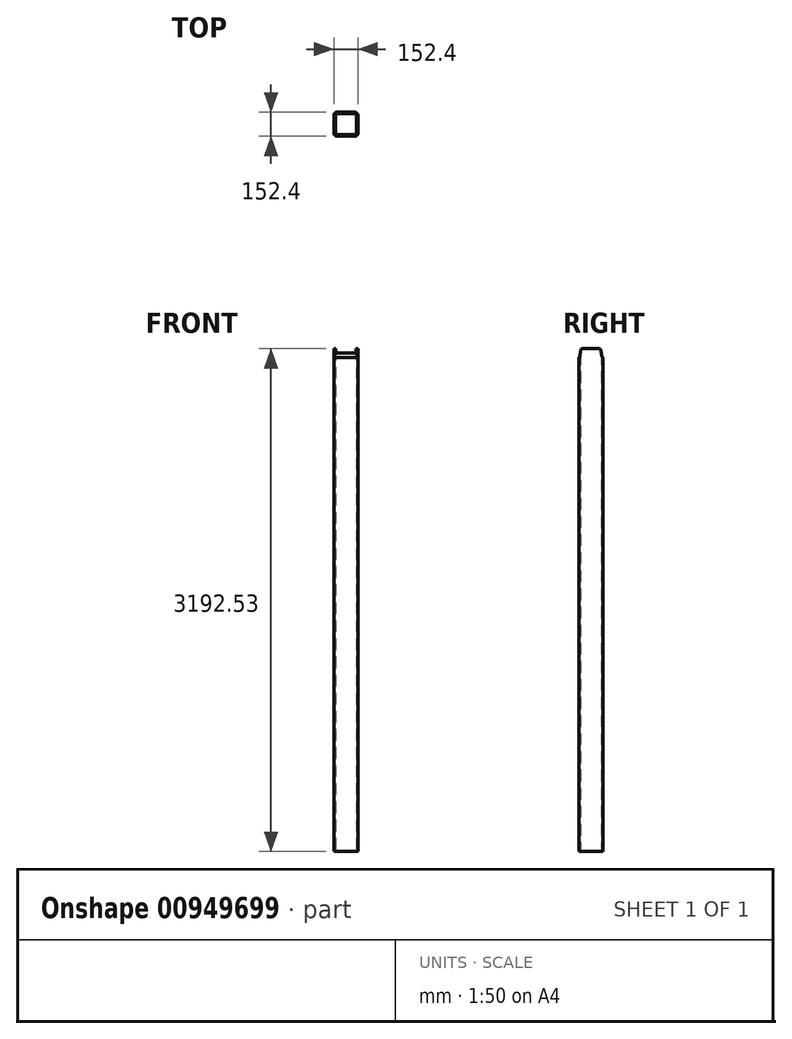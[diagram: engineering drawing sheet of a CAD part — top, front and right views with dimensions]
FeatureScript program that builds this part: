
annotation { "Feature Type Name" : "Feature", "Feature Type Description" : "" }
export const myFeature = defineFeature(function(context is Context, id is Id, definition is map)
    precondition{}
    {
        {
            var Q0;
            Q0=qCreatedBy(makeId("Top.planeOp"),FACE);
            var sketch = newSketch(context, id + "F0", { "sketchPlane" : qUnion([Q0])});
            skLineSegment(sketch, "E0.bottom", {"start": v(-57.15, -76.2) * mm, "end": v(57.15, -76.2) * mm});
            skLineSegment(sketch, "E0.top", {"start": v(-57.15, 76.2) * mm, "end": v(57.15, 76.2) * mm});
            skLineSegment(sketch, "E0.left", {"start": v(-76.2, -57.15) * mm, "end": v(-76.2, 57.15) * mm});
            skLineSegment(sketch, "E0.right", {"start": v(76.2, -57.15) * mm, "end": v(76.2, 57.15) * mm});
            skPoint(sketch, "E0.middle", {"position": v(0, 0) * mm});
            skLineSegment(sketch, "E1.bottom", {"start": v(-57.15, -66.68) * mm, "end": v(57.15, -66.68) * mm});
            skLineSegment(sketch, "E1.top", {"start": v(-57.15, 66.68) * mm, "end": v(57.15, 66.68) * mm});
            skLineSegment(sketch, "E1.left", {"start": v(-66.68, -57.15) * mm, "end": v(-66.68, 57.15) * mm});
            skLineSegment(sketch, "E1.right", {"start": v(66.68, -57.15) * mm, "end": v(66.68, 57.15) * mm});
            skPoint(sketch, "E2.visualSharp", {"position": v(-76.2, 76.2) * mm});
            skArc(sketch, "E2.filletArc", {"start": v(-57.15, 76.2) * mm, "mid": v(-70.62, 70.62) * mm, "end": v(-76.2, 57.15) * mm});
            skPoint(sketch, "E3.visualSharp", {"position": v(-76.2, -76.2) * mm});
            skArc(sketch, "E3.filletArc", {"start": v(-76.2, -57.15) * mm, "mid": v(-70.62, -70.62) * mm, "end": v(-57.15, -76.2) * mm});
            skPoint(sketch, "E4.visualSharp", {"position": v(76.2, -76.2) * mm});
            skArc(sketch, "E4.filletArc", {"start": v(57.15, -76.2) * mm, "mid": v(70.62, -70.62) * mm, "end": v(76.2, -57.15) * mm});
            skPoint(sketch, "E5.visualSharp", {"position": v(76.2, 76.2) * mm});
            skArc(sketch, "E5.filletArc", {"start": v(76.2, 57.15) * mm, "mid": v(70.62, 70.62) * mm, "end": v(57.15, 76.2) * mm});
            skPoint(sketch, "E6.visualSharp", {"position": v(-66.68, 66.68) * mm});
            skArc(sketch, "E6.filletArc", {"start": v(-57.15, 66.68) * mm, "mid": v(-63.89, 63.89) * mm, "end": v(-66.68, 57.15) * mm});
            skPoint(sketch, "E7.visualSharp", {"position": v(-66.68, -66.68) * mm});
            skArc(sketch, "E7.filletArc", {"start": v(-66.68, -57.15) * mm, "mid": v(-63.89, -63.89) * mm, "end": v(-57.15, -66.68) * mm});
            skPoint(sketch, "E8.visualSharp", {"position": v(66.68, -66.68) * mm});
            skArc(sketch, "E8.filletArc", {"start": v(57.15, -66.68) * mm, "mid": v(63.89, -63.89) * mm, "end": v(66.68, -57.15) * mm});
            skPoint(sketch, "E9.visualSharp", {"position": v(66.68, 66.68) * mm});
            skArc(sketch, "E9.filletArc", {"start": v(66.68, 57.15) * mm, "mid": v(63.89, 63.89) * mm, "end": v(57.15, 66.68) * mm});
            skSolve(sketch);
        }
        {
            var Q0;
            Q0=qSketchRegion(id+"F0",true);
            extrude(context, id + "F1", {"entities" : qUnion([Q0]), "depth" : 3200.4 * mm, "offsetDistance" : 25.4 * mm});
        }
        {
            var Q0;
            Q0=qCreatedBy(makeId("Right.planeOp"),FACE);
            var sketch = newSketch(context, id + "F2", { "sketchPlane" : qUnion([Q0])});
            skLineSegment(sketch, "E10", {"start": v(-76.2, 3200.4) * mm, "end": v(76.2, 3200.4) * mm});
            skLineSegment(sketch, "E11", {"start": v(76.2, 3200.4) * mm, "end": v(76.2, 3136.98) * mm});
            skLineSegment(sketch, "E12", {"start": v(-76.2, 3200.4) * mm, "end": v(-76.2, 3136.98) * mm});
            skLineSegment(sketch, "E13", {"start": v(-63.12, 3184.83) * mm, "end": v(-70.65, 3141.64) * mm});
            skLineSegment(sketch, "E14", {"start": v(63.12, 3184.83) * mm, "end": v(70.65, 3141.64) * mm});
            skLineSegment(sketch, "E15", {"start": v(-53.98, 3192.53) * mm, "end": v(53.98, 3192.53) * mm});
            skArc(sketch, "E16.filletArc", {"start": v(-76.2, 3136.98) * mm, "mid": v(-72.57, 3138.3) * mm, "end": v(-70.65, 3141.64) * mm});
            skArc(sketch, "E17.filletArc", {"start": v(70.65, 3141.64) * mm, "mid": v(72.57, 3138.3) * mm, "end": v(76.2, 3136.98) * mm});
            skArc(sketch, "E18.filletArc", {"start": v(-53.98, 3192.53) * mm, "mid": v(-59.95, 3190.35) * mm, "end": v(-63.12, 3184.83) * mm});
            skArc(sketch, "E19.filletArc", {"start": v(63.12, 3184.83) * mm, "mid": v(59.95, 3190.35) * mm, "end": v(53.98, 3192.53) * mm});
            skSolve(sketch);
        }
        {
            var Q0;
            Q0=qSketchRegion(id+"F2",true);
            extrude(context, id + "F3", {"entities" : qUnion([Q0]), "operationType" : NewBodyOperationType.REMOVE, "endBound" : BoundingType.THROUGH_ALL, "oppositeDirection" : true, "depth" : 25.4 * mm, "offsetDistance" : 25.4 * mm, "hasSecondDirection" : true, "secondDirectionBound" : SecondDirectionBoundingType.THROUGH_ALL, "secondDirectionOppositeDirection" : false, "secondDirectionDepth" : 25.4 * mm});
        }
    });
